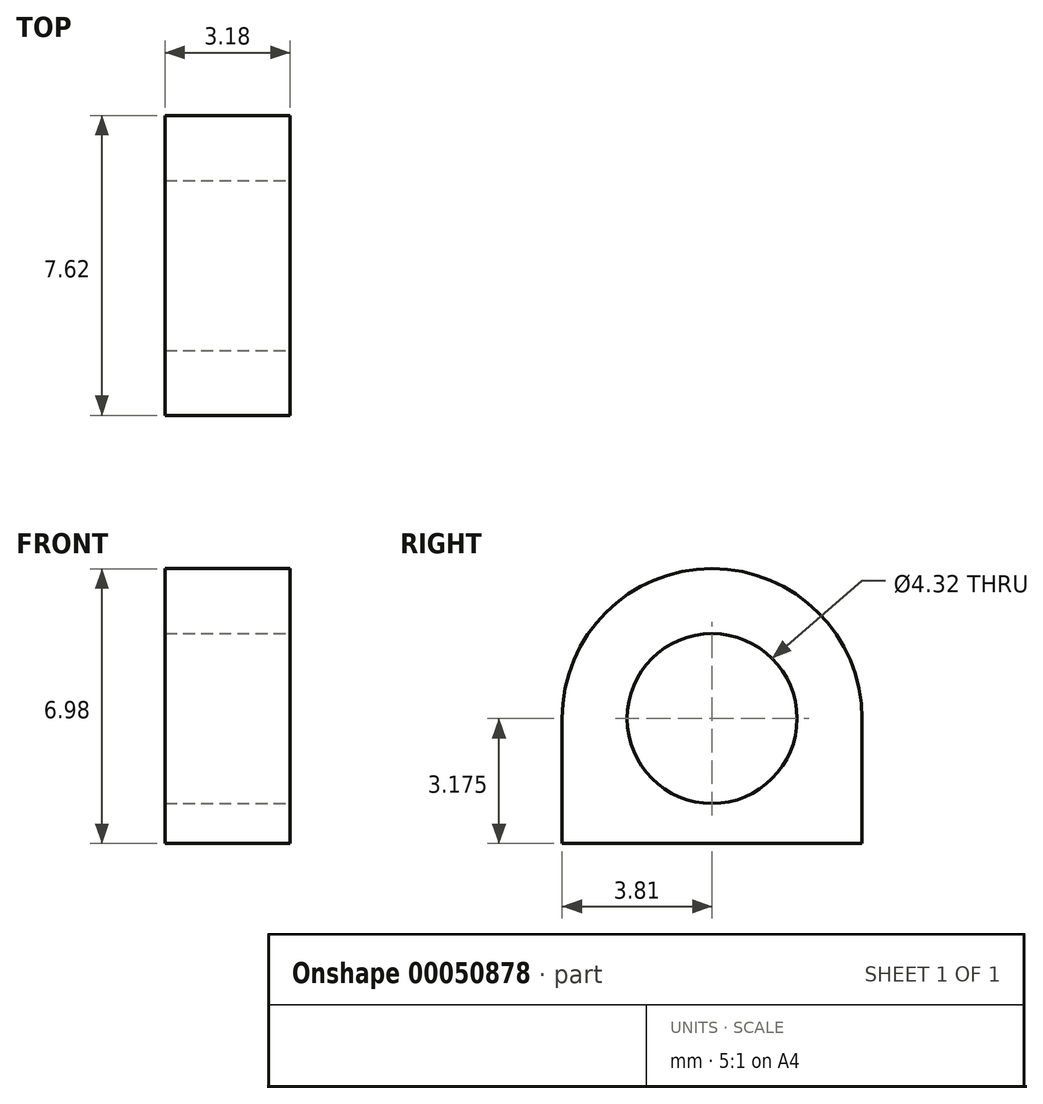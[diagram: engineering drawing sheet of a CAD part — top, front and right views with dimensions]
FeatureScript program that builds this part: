
annotation { "Feature Type Name" : "Feature", "Feature Type Description" : "" }
export const myFeature = defineFeature(function(context is Context, id is Id, definition is map)
    precondition{}
    {
        {
            var Q0;
            Q0=qCreatedBy(makeId("Top.planeOp"),FACE);
            var sketch = newSketch(context, id + "F0", { "sketchPlane" : qUnion([Q0])});
            skLineSegment(sketch, "E0.bottom", {"start": v(0, 0) * mm, "end": v(-3.18, 0) * mm});
            skLineSegment(sketch, "E0.top", {"start": v(0, -7.62) * mm, "end": v(-3.17, -7.62) * mm});
            skLineSegment(sketch, "E0.left", {"start": v(0, 0) * mm, "end": v(0, -7.62) * mm});
            skLineSegment(sketch, "E0.right", {"start": v(-3.18, 0) * mm, "end": v(-3.17, -7.62) * mm});
            skSolve(sketch);
        }
        {
            var Q0;
            Q0 = qSketchRegion(id + "F0", true);
            extrude(context, id + "F1", {"entities" : qUnion([Q0]), "depth" : 3.17 * mm});
        }
        {
            var Q0;
            Q0=makeQuery(id+"F1.opExtrude","SWEPT_FACE",FACE,{"disambiguationData":[OSD([sQuery(id+"F0.wireOp",EDGE,"E0.left")])]});
            var sketch = newSketch(context, id + "F2", { "sketchPlane" : qUnion([Q0])});
            skArc(sketch, "E1", {"start": v(0, 3.18) * mm, "mid": v(-3.81, 6.98) * mm, "end": v(-7.62, 3.17) * mm});
            skLineSegment(sketch, "E2", {"start": v(-7.62, 3.18) * mm, "end": v(0, 3.18) * mm});
            skSolve(sketch);
        }
        {
            var Q0;
            Q0 = qSketchRegion(id + "F2", true);
            extrude(context, id + "F3", {"entities" : qUnion([Q0]), "operationType" : NewBodyOperationType.ADD, "oppositeDirection" : true, "depth" : 3.17 * mm});
        }
        {
            var Q0;
            Q0=makeQuery(id+"F3.boolean.opBoolean","MERGE",FACE,{"derivedFrom":[makeQuery(id+"F1.opExtrude","SWEPT_FACE",FACE,{"disambiguationData":[OSD([sQuery(id+"F0.wireOp",EDGE,"E0.left")])]}),makeQuery(id+"F3.opExtrude","CAP_FACE",FACE,{"disambiguationData":[OSD([sQuery(id+"F2.wireOp",EDGE,"E1"),sQuery(id+"F2.wireOp",EDGE,"E2")])],"isStart":true})]});
            var sketch = newSketch(context, id + "F4", { "sketchPlane" : qUnion([Q0])});
            skLineSegment(sketch, "E3", {"start": v(-7.62, 3.18) * mm, "end": v(0, 3.18) * mm, "construction": true});
            skLineSegment(sketch, "E4", {"start": v(-3.81, 6.98) * mm, "end": v(-3.81, 0) * mm, "construction": true});
            skCircle(sketch, "E5", {"center": v(-3.8, 3.18) * mm, "radius": 2.16 * mm});
            skSolve(sketch);
        }
        {
            var Q0;
            Q0=makeQuery(id+"F4.imprint","IMPRINT",FACE,{"disambiguationData":[TD([[makeQuery(id+"F4.imprint","IMPRINT",EDGE,{"derivedFrom":sQuery(id+"F4.wireOp",EDGE,"E5")}),1.0]])]});
            extrude(context, id + "F5", {"entities" : qUnion([Q0]), "operationType" : NewBodyOperationType.REMOVE, "oppositeDirection" : true, "depth" : 25.4 * mm});
        }
    });
